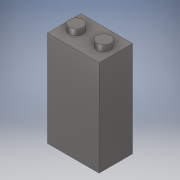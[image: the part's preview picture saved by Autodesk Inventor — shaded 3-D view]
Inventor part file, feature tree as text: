
AUTODESK INVENTOR PART (.ipt)
format: ipt  version: 2017 (Build 210142000, 142)  size: 112,640 bytes
history: native  units: mm
features: extrude x2, sketch x2
ambient origin geometry x8: Origin, YZ Plane, XZ Plane, XY Plane, X Axis, Y Axis, Z Axis, Center Point
bodies: Volumenkörper1 (feature_tree)
feature tree (4):
  extrude  "Extrusion1"  Depth=26.2mm
  extrude  "Extrusion2"  Depth=3.0mm
  sketch  "Skizze1"  dims[d0=48.5mm d1=26.2mm]
  sketch  "Skizze3"  dims[d2=17.0mm d3=0.0mm d7=13.1mm d8=7.0mm d9=8.5mm d10=7.0mm d11=3.0mm d12=0.0mm]
